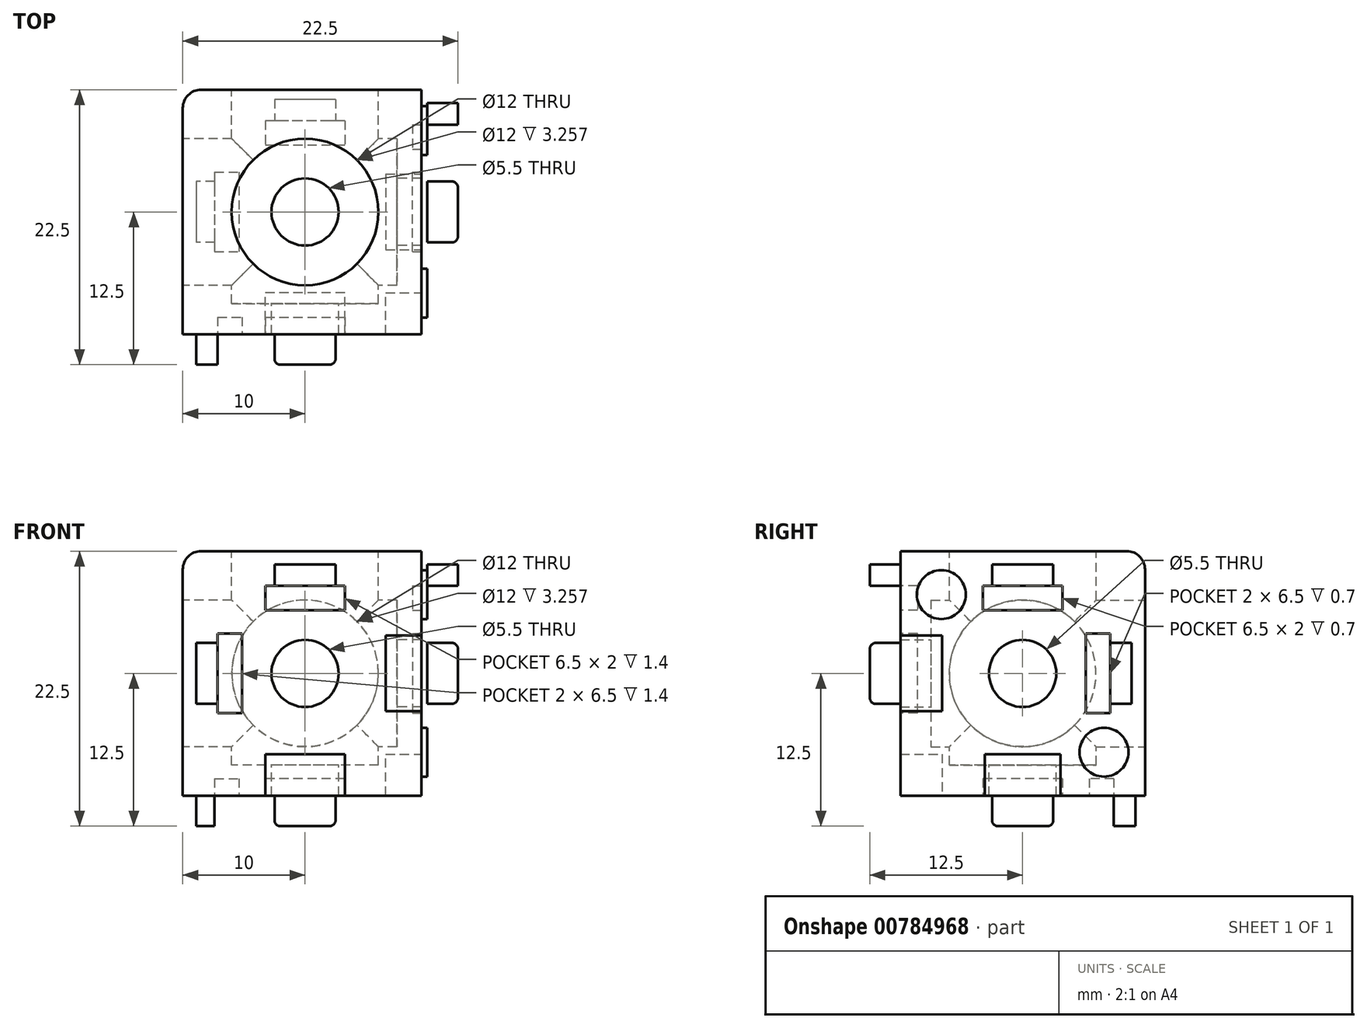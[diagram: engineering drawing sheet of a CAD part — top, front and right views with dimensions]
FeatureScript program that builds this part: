
annotation { "Feature Type Name" : "Feature", "Feature Type Description" : "" }
export const myFeature = defineFeature(function(context is Context, id is Id, definition is map)
    precondition{}
    {
        {
            var Q0;
            Q0=qCreatedBy(makeId("Top.planeOp"),FACE);
            var sketch = newSketch(context, id + "F0", { "sketchPlane" : qUnion([Q0])});
            skLineSegment(sketch, "E0.bottom", {"start": v(10, -10) * mm, "end": v(-10, -10) * mm});
            skLineSegment(sketch, "E0.top", {"start": v(10, 10) * mm, "end": v(-10, 10) * mm});
            skLineSegment(sketch, "E0.left", {"start": v(10, -10) * mm, "end": v(10, 10) * mm});
            skLineSegment(sketch, "E0.right", {"start": v(-10, -10) * mm, "end": v(-10, 10) * mm});
            skPoint(sketch, "E0.middle", {"position": v(0, 0) * mm});
            skLineSegment(sketch, "E1", {"start": v(-10, 10) * mm, "end": v(10, -10) * mm, "construction": true});
            skLineSegment(sketch, "E2", {"start": v(10, 10) * mm, "end": v(-10, -10) * mm, "construction": true});
            skSolve(sketch);
        }
        {
            var Q0;
            Q0=makeQuery(id+"F0.imprint","IMPRINT",FACE,{"disambiguationData":[TD([[makeQuery(id+"F0.imprint","IMPRINT",EDGE,{"derivedFrom":sQuery(id+"F0.wireOp",EDGE,"E0.bottom")}),-1.0]])]});
            extrude(context, id + "F1", {"entities" : qUnion([Q0]), "endBound" : BoundingType.SYMMETRIC, "depth" : 20 * mm, "offsetDistance" : 25 * mm});
        }
        {
            var Q0;
            Q0=makeQuery(id+"F1.opExtrude","CAP_FACE",FACE,{"disambiguationData":[OSD([sQuery(id+"F0.wireOp",EDGE,"E0.bottom"),sQuery(id+"F0.wireOp",EDGE,"E0.top"),sQuery(id+"F0.wireOp",EDGE,"E0.left"),sQuery(id+"F0.wireOp",EDGE,"E0.right")])],"isStart":false});
            var sketch = newSketch(context, id + "F2", { "sketchPlane" : qUnion([Q0])});
            skCircle(sketch, "E3", {"center": v(0, 0) * mm, "radius": 6 * mm});
            skLineSegment(sketch, "E4", {"start": v(-10, 10) * mm, "end": v(10, -10) * mm, "construction": true});
            skLineSegment(sketch, "E5", {"start": v(10, 10) * mm, "end": v(-10, -10) * mm, "construction": true});
            skSolve(sketch);
        }
        {
            var Q0;
            Q0=makeQuery(id+"F2.imprint","IMPRINT",FACE,{"disambiguationData":[TD([[makeQuery(id+"F2.imprint","IMPRINT",EDGE,{"derivedFrom":sQuery(id+"F2.wireOp",EDGE,"E3")}),1.0]])]});
            extrude(context, id + "F3", {"entities" : qUnion([Q0]), "operationType" : NewBodyOperationType.REMOVE, "oppositeDirection" : true, "depth" : 17.5 * mm, "offsetDistance" : 25 * mm});
        }
        {
            var Q0;
            Q0=makeQuery(id+"F1.opExtrude","SWEPT_FACE",FACE,{"disambiguationData":[OSD([sQuery(id+"F0.wireOp",EDGE,"E0.top")])]});
            var sketch = newSketch(context, id + "F4", { "sketchPlane" : qUnion([Q0])});
            skCircle(sketch, "E6", {"center": v(0, 0) * mm, "radius": 6 * mm});
            skLineSegment(sketch, "E7", {"start": v(-10, 10) * mm, "end": v(10, -10) * mm, "construction": true});
            skLineSegment(sketch, "E8", {"start": v(-10, -10) * mm, "end": v(10, 10) * mm, "construction": true});
            skSolve(sketch);
        }
        {
            var Q0;
            Q0=makeQuery(id+"F4.imprint","IMPRINT",FACE,{"disambiguationData":[TD([[makeQuery(id+"F4.imprint","IMPRINT",EDGE,{"derivedFrom":sQuery(id+"F4.wireOp",EDGE,"E6")}),1.0]])]});
            extrude(context, id + "F5", {"entities" : qUnion([Q0]), "operationType" : NewBodyOperationType.REMOVE, "oppositeDirection" : true, "depth" : 17.5 * mm, "offsetDistance" : 25 * mm});
        }
        {
            var Q0;
            Q0=makeQuery(id+"F1.opExtrude","SWEPT_FACE",FACE,{"disambiguationData":[OSD([sQuery(id+"F0.wireOp",EDGE,"E0.right")])]});
            var sketch = newSketch(context, id + "F6", { "sketchPlane" : qUnion([Q0])});
            skCircle(sketch, "E9", {"center": v(0, 0) * mm, "radius": 6 * mm});
            skLineSegment(sketch, "E10", {"start": v(-10, 10) * mm, "end": v(10, -10) * mm, "construction": true});
            skLineSegment(sketch, "E11", {"start": v(10, 10) * mm, "end": v(-10, -10) * mm});
            skSolve(sketch);
        }
        {
            var Q0;
            Q0=makeQuery(id+"F6.imprint","IMPRINT",FACE,{"disambiguationData":[TD([[makeQuery(id+"F6.imprint","IMPRINT",EDGE,{"derivedFrom":sQuery(id+"F6.wireOp",EDGE,"E9")}),1.0]])]});
            extrude(context, id + "F7", {"entities" : qUnion([Q0]), "operationType" : NewBodyOperationType.REMOVE, "oppositeDirection" : true, "depth" : 17.5 * mm, "offsetDistance" : 25 * mm});
        }
        {
            var Q0;
            Q0=makeQuery(id+"F3.boolean.opBoolean","COPY",FACE,{"derivedFrom":makeQuery(id+"F3.opExtrude","CAP_FACE",FACE,{"disambiguationData":[OSD([sQuery(id+"F2.wireOp",EDGE,"E3")])],"isStart":false})});
            var sketch = newSketch(context, id + "F8", { "sketchPlane" : qUnion([Q0])});
            skPoint(sketch, "E12", {"position": v(0, 0) * mm});
            skSolve(sketch);
        }
        {
            var Q0;
            Q0=sQuery(id+"F8.wireOp",VERTEX,"E12");
            var Q1;
            Q1=makeQuery(id+"F1.opExtrude","SWEPT_BODY",BODY,{"disambiguationData":[OSD([sQuery(id+"F0.wireOp",EDGE,"E0.bottom"),sQuery(id+"F0.wireOp",EDGE,"E0.top"),sQuery(id+"F0.wireOp",EDGE,"E0.left"),sQuery(id+"F0.wireOp",EDGE,"E0.right")])]});
            hole(context, id + "F9", {"style" : HoleStyle.SIMPLE, "endStyle" : HoleEndStyle.THROUGH, "holeDiameter" : 5.5 * mm, "majorDiameter" : 5 * mm, "isTappedThrough" : true, "tappedDepth" : 12 * mm, "tapClearance" : 3, "locations" : qUnion([Q0]), "scope" : qUnion([Q1])});
        }
        {
            var Q0;
            Q0=makeQuery(id+"F5.boolean.opBoolean","COPY",FACE,{"derivedFrom":makeQuery(id+"F5.opExtrude","CAP_FACE",FACE,{"disambiguationData":[OSD([sQuery(id+"F4.wireOp",EDGE,"E6")])],"isStart":false})});
            var sketch = newSketch(context, id + "F10", { "sketchPlane" : qUnion([Q0])});
            skPoint(sketch, "E13", {"position": v(0, 0) * mm});
            skSolve(sketch);
        }
        {
            var Q0;
            Q0=sQuery(id+"F10.wireOp",VERTEX,"E13");
            var Q1;
            Q1=makeQuery(id+"F1.opExtrude","SWEPT_BODY",BODY,{"disambiguationData":[OSD([sQuery(id+"F0.wireOp",EDGE,"E0.bottom"),sQuery(id+"F0.wireOp",EDGE,"E0.top"),sQuery(id+"F0.wireOp",EDGE,"E0.left"),sQuery(id+"F0.wireOp",EDGE,"E0.right")])]});
            hole(context, id + "F11", {"style" : HoleStyle.SIMPLE, "endStyle" : HoleEndStyle.THROUGH, "holeDiameter" : 5.5 * mm, "majorDiameter" : 5 * mm, "isTappedThrough" : true, "tappedDepth" : 12 * mm, "tapClearance" : 3, "locations" : qUnion([Q0]), "scope" : qUnion([Q1])});
        }
        {
            var Q0;
            Q0=makeQuery(id+"F7.boolean.opBoolean","COPY",FACE,{"derivedFrom":makeQuery(id+"F7.opExtrude","CAP_FACE",FACE,{"disambiguationData":[OSD([sQuery(id+"F6.wireOp",EDGE,"E9")])],"isStart":false})});
            var sketch = newSketch(context, id + "F12", { "sketchPlane" : qUnion([Q0])});
            skPoint(sketch, "E14", {"position": v(0, 0) * mm});
            skSolve(sketch);
        }
        {
            var Q0;
            Q0=sQuery(id+"F12.wireOp",VERTEX,"E14");
            var Q1;
            Q1=makeQuery(id+"F1.opExtrude","SWEPT_BODY",BODY,{"disambiguationData":[OSD([sQuery(id+"F0.wireOp",EDGE,"E0.bottom"),sQuery(id+"F0.wireOp",EDGE,"E0.top"),sQuery(id+"F0.wireOp",EDGE,"E0.left"),sQuery(id+"F0.wireOp",EDGE,"E0.right")])]});
            hole(context, id + "F13", {"style" : HoleStyle.SIMPLE, "endStyle" : HoleEndStyle.THROUGH, "holeDiameter" : 5.5 * mm, "majorDiameter" : 5 * mm, "isTappedThrough" : true, "tappedDepth" : 12 * mm, "tapClearance" : 3, "locations" : qUnion([Q0]), "scope" : qUnion([Q1])});
        }
        {
            var Q0;
            Q0=makeQuery(id+"F1.opExtrude","SWEPT_FACE",FACE,{"disambiguationData":[OSD([sQuery(id+"F0.wireOp",EDGE,"E0.left")])]});
            var sketch = newSketch(context, id + "F14", { "sketchPlane" : qUnion([Q0])});
            skLineSegment(sketch, "E15", {"start": v(10, 0) * mm, "end": v(-10, 0) * mm, "construction": true});
            skLineSegment(sketch, "E16", {"start": v(0, 10) * mm, "end": v(0, -10) * mm, "construction": true});
            skCircle(sketch, "E17", {"center": v(6.65, 6.45) * mm, "radius": 2 * mm});
            skCircle(sketch, "E18.MirrorC", {"center": v(6.65, -6.45) * mm, "radius": 2 * mm});
            skCircle(sketch, "E19.MirrorC", {"center": v(-6.65, -6.45) * mm, "radius": 2 * mm});
            skCircle(sketch, "E20.MirrorC", {"center": v(-6.65, 6.45) * mm, "radius": 2 * mm});
            skSolve(sketch);
        }
        {
            var Q0;
            Q0=makeQuery(id+"F14.imprint","IMPRINT",FACE,{"disambiguationData":[TD([[makeQuery(id+"F14.imprint","IMPRINT",EDGE,{"derivedFrom":sQuery(id+"F14.wireOp",EDGE,"E17")}),1.0]])]});
            var Q1;
            Q1=makeQuery(id+"F14.imprint","IMPRINT",FACE,{"disambiguationData":[TD([[makeQuery(id+"F14.imprint","IMPRINT",EDGE,{"derivedFrom":sQuery(id+"F14.wireOp",EDGE,"E18.MirrorC")}),-1.0]])]});
            var Q2;
            Q2=makeQuery(id+"F14.imprint","IMPRINT",FACE,{"disambiguationData":[TD([[makeQuery(id+"F14.imprint","IMPRINT",EDGE,{"derivedFrom":sQuery(id+"F14.wireOp",EDGE,"E19.MirrorC")}),1.0]])]});
            var Q3;
            Q3=makeQuery(id+"F14.imprint","IMPRINT",FACE,{"disambiguationData":[TD([[makeQuery(id+"F14.imprint","IMPRINT",EDGE,{"derivedFrom":sQuery(id+"F14.wireOp",EDGE,"E20.MirrorC")}),-1.0]])]});
            extrude(context, id + "F15", {"entities" : qUnion([Q0, Q1, Q2, Q3]), "operationType" : NewBodyOperationType.REMOVE, "oppositeDirection" : true, "depth" : 0.5 * mm, "offsetDistance" : 25 * mm});
        }
        {
            var Q0;
            Q0=makeQuery(id+"F1.opExtrude","SWEPT_FACE",FACE,{"disambiguationData":[OSD([sQuery(id+"F0.wireOp",EDGE,"E0.left")])]});
            var sketch = newSketch(context, id + "F16", { "sketchPlane" : qUnion([Q0])});
            skLineSegment(sketch, "E21.bottom", {"start": v(7.15, -2.5) * mm, "end": v(8.9, -2.5) * mm});
            skLineSegment(sketch, "E21.top", {"start": v(7.15, 2.5) * mm, "end": v(8.9, 2.5) * mm});
            skLineSegment(sketch, "E21.left", {"start": v(7.15, -2.5) * mm, "end": v(7.15, 2.5) * mm});
            skLineSegment(sketch, "E21.right", {"start": v(8.9, -2.5) * mm, "end": v(8.9, 2.5) * mm});
            skPoint(sketch, "E21.middle", {"position": v(8.03, 0) * mm});
            skPoint(sketch, "E21.middle.positionSnap0", {"position": v(10, 0) * mm});
            skPoint(sketch, "E21.centerSnap0", {"position": v(10, 0) * mm});
            skLineSegment(sketch, "E22.bottom", {"start": v(-2.5, 7.15) * mm, "end": v(2.5, 7.15) * mm});
            skLineSegment(sketch, "E22.top", {"start": v(-2.5, 8.9) * mm, "end": v(2.5, 8.9) * mm});
            skLineSegment(sketch, "E22.left", {"start": v(-2.5, 7.15) * mm, "end": v(-2.5, 8.9) * mm});
            skLineSegment(sketch, "E22.right", {"start": v(2.5, 7.15) * mm, "end": v(2.5, 8.9) * mm});
            skPoint(sketch, "E22.middle", {"position": v(0, 8.02) * mm});
            skPoint(sketch, "E22.middle.positionSnap0", {"position": v(0, 10) * mm});
            skPoint(sketch, "E22.centerSnap0", {"position": v(0, 10) * mm});
            skSolve(sketch);
        }
        {
            var Q0;
            Q0 = qSketchRegion(id + "F16", true);
            extrude(context, id + "F17", {"entities" : qUnion([Q0]), "operationType" : NewBodyOperationType.ADD, "depth" : 2.5 * mm, "offsetDistance" : 25 * mm});
        }
        {
            var Q0;
            Q0=makeQuery(id+"F1.opExtrude","SWEPT_FACE",FACE,{"disambiguationData":[OSD([sQuery(id+"F0.wireOp",EDGE,"E0.left")])]});
            var sketch = newSketch(context, id + "F18", { "sketchPlane" : qUnion([Q0])});
            skLineSegment(sketch, "E23.bottom", {"start": v(7.15, 3.25) * mm, "end": v(5.15, 3.25) * mm});
            skLineSegment(sketch, "E23.top", {"start": v(7.15, -3.25) * mm, "end": v(5.15, -3.25) * mm});
            skLineSegment(sketch, "E23.left", {"start": v(7.15, 3.25) * mm, "end": v(7.15, -3.25) * mm});
            skLineSegment(sketch, "E23.right", {"start": v(5.15, 3.25) * mm, "end": v(5.15, -3.25) * mm});
            skLineSegment(sketch, "E24.bottom", {"start": v(-3.25, 7.15) * mm, "end": v(3.25, 7.15) * mm});
            skLineSegment(sketch, "E24.top", {"start": v(-3.25, 5.15) * mm, "end": v(3.25, 5.15) * mm});
            skLineSegment(sketch, "E24.left", {"start": v(-3.25, 7.15) * mm, "end": v(-3.25, 5.15) * mm});
            skLineSegment(sketch, "E24.right", {"start": v(3.25, 7.15) * mm, "end": v(3.25, 5.15) * mm});
            skSolve(sketch);
        }
        {
            var Q0;
            Q0=makeQuery(id+"F18.imprint","IMPRINT",FACE,{"disambiguationData":[TD([[makeQuery(id+"F18.imprint","IMPRINT",EDGE,{"derivedFrom":sQuery(id+"F18.wireOp",EDGE,"E24.top")}),1.0]])]});
            var Q1;
            {var subQ3=sQuery(id+"F18.wireOp",EDGE,"E23.bottom");Q1=makeQuery(id+"F18.imprint","IMPRINT",FACE,{"disambiguationData":[TD([[makeQuery(id+"F18.imprint","IMPRINT",EDGE,{"derivedFrom":subQ3}),1.0]])]});}
            extrude(context, id + "F19", {"entities" : qUnion([Q0, Q1]), "operationType" : NewBodyOperationType.REMOVE, "oppositeDirection" : true, "depth" : 1.2 * mm, "offsetDistance" : 25 * mm});
        }
        {
            var Q0;
            Q0=makeQuery(id+"F1.opExtrude","SWEPT_FACE",FACE,{"disambiguationData":[OSD([sQuery(id+"F0.wireOp",EDGE,"E0.left")])]});
            var sketch = newSketch(context, id + "F20", { "sketchPlane" : qUnion([Q0])});
            skLineSegment(sketch, "E25.bottom", {"start": v(3.1, -10) * mm, "end": v(-3.1, -10) * mm});
            skLineSegment(sketch, "E25.top", {"start": v(3.1, -6.6) * mm, "end": v(-3.1, -6.6) * mm});
            skLineSegment(sketch, "E25.left", {"start": v(3.1, -10) * mm, "end": v(3.1, -6.6) * mm});
            skLineSegment(sketch, "E25.right", {"start": v(-3.1, -10) * mm, "end": v(-3.1, -6.6) * mm});
            skLineSegment(sketch, "E26.bottom", {"start": v(-10, -3.1) * mm, "end": v(-6.6, -3.1) * mm});
            skLineSegment(sketch, "E26.top", {"start": v(-10, 3.1) * mm, "end": v(-6.6, 3.1) * mm});
            skLineSegment(sketch, "E26.left", {"start": v(-10, -3.1) * mm, "end": v(-10, 3.1) * mm});
            skLineSegment(sketch, "E26.right", {"start": v(-6.6, -3.1) * mm, "end": v(-6.6, 3.1) * mm});
            skSolve(sketch);
        }
        {
            var Q0;
            Q0 = qSketchRegion(id + "F20", true);
            extrude(context, id + "F21", {"entities" : qUnion([Q0]), "operationType" : NewBodyOperationType.REMOVE, "oppositeDirection" : true, "depth" : 3.4 * mm, "offsetDistance" : 25 * mm});
        }
        {
            var Q0;
            Q0=makeQuery(id+"F17.opExtrude","CAP_EDGE",EDGE,{"disambiguationData":[OSD([sQuery(id+"F16.wireOp",EDGE,"E22.left")])],"isStart":false});
            var Q1;
            Q1=makeQuery(id+"F17.opExtrude","CAP_EDGE",EDGE,{"disambiguationData":[OSD([sQuery(id+"F16.wireOp",EDGE,"E22.right")])],"isStart":false});
            var Q2;
            Q2=makeQuery(id+"F17.opExtrude","CAP_EDGE",EDGE,{"disambiguationData":[OSD([sQuery(id+"F16.wireOp",EDGE,"E21.top")])],"isStart":false});
            var Q3;
            Q3=makeQuery(id+"F17.opExtrude","CAP_EDGE",EDGE,{"disambiguationData":[OSD([sQuery(id+"F16.wireOp",EDGE,"E21.bottom")])],"isStart":false});
            fillet(context, id + "F22", {"entities" : qUnion([Q0, Q1, Q2, Q3]), "radius" : 0.5 * mm, "tangentPropagation" : true, "allowEdgeOverflow" : false});
        }
        {
            var Q0;
            Q0=makeQuery(id+"F1.opExtrude","CAP_FACE",FACE,{"disambiguationData":[OSD([sQuery(id+"F0.wireOp",EDGE,"E0.bottom"),sQuery(id+"F0.wireOp",EDGE,"E0.top"),sQuery(id+"F0.wireOp",EDGE,"E0.left"),sQuery(id+"F0.wireOp",EDGE,"E0.right")])],"isStart":true});
            var sketch = newSketch(context, id + "F23", { "sketchPlane" : qUnion([Q0])});
            skLineSegment(sketch, "E27", {"start": v(0, -10) * mm, "end": v(0, 10) * mm, "construction": true});
            skLineSegment(sketch, "E28", {"start": v(-10, 0) * mm, "end": v(6.6, 0) * mm, "construction": true});
            skLineSegment(sketch, "E29.bottom", {"start": v(2.5, -9.2) * mm, "end": v(-2.5, -9.2) * mm});
            skLineSegment(sketch, "E29.top", {"start": v(2.5, -7.46) * mm, "end": v(-2.5, -7.46) * mm});
            skLineSegment(sketch, "E29.left", {"start": v(2.5, -9.2) * mm, "end": v(2.5, -7.46) * mm});
            skLineSegment(sketch, "E29.right", {"start": v(-2.5, -9.2) * mm, "end": v(-2.5, -7.46) * mm});
            skLineSegment(sketch, "E30.bottom", {"start": v(-3.25, -7.46) * mm, "end": v(3.25, -7.46) * mm});
            skLineSegment(sketch, "E30.top", {"start": v(-3.25, -5.46) * mm, "end": v(3.25, -5.46) * mm});
            skLineSegment(sketch, "E30.left", {"start": v(-3.25, -7.46) * mm, "end": v(-3.25, -5.46) * mm});
            skLineSegment(sketch, "E30.right", {"start": v(3.25, -7.46) * mm, "end": v(3.25, -5.46) * mm});
            skSolve(sketch);
        }
        {
            var Q0;
            Q0=makeQuery(id+"F23.imprint","IMPRINT",FACE,{"disambiguationData":[TD([[makeQuery(id+"F23.imprint","IMPRINT",EDGE,{"derivedFrom":sQuery(id+"F23.wireOp",EDGE,"E29.bottom")}),-1.0]])]});
            extrude(context, id + "F24", {"entities" : qUnion([Q0]), "operationType" : NewBodyOperationType.ADD, "depth" : 2.5 * mm, "offsetDistance" : 25 * mm});
        }
        {
            var Q0;
            Q0=makeQuery(id+"F1.opExtrude","CAP_FACE",FACE,{"disambiguationData":[OSD([sQuery(id+"F0.wireOp",EDGE,"E0.bottom"),sQuery(id+"F0.wireOp",EDGE,"E0.top"),sQuery(id+"F0.wireOp",EDGE,"E0.left"),sQuery(id+"F0.wireOp",EDGE,"E0.right")])],"isStart":true});
            var sketch = newSketch(context, id + "F25", { "sketchPlane" : qUnion([Q0])});
            skLineSegment(sketch, "E31.bottom", {"start": v(3.25, -7.46) * mm, "end": v(-3.25, -7.46) * mm});
            skLineSegment(sketch, "E31.top", {"start": v(3.25, -5.46) * mm, "end": v(-3.25, -5.46) * mm});
            skLineSegment(sketch, "E31.left", {"start": v(3.25, -7.46) * mm, "end": v(3.25, -5.46) * mm});
            skLineSegment(sketch, "E31.right", {"start": v(-3.25, -7.46) * mm, "end": v(-3.25, -5.46) * mm});
            skSolve(sketch);
        }
        {
            var Q0;
            Q0=makeQuery(id+"F25.imprint","IMPRINT",FACE,{"disambiguationData":[TD([[makeQuery(id+"F25.imprint","IMPRINT",EDGE,{"derivedFrom":sQuery(id+"F25.wireOp",EDGE,"E31.top")}),1.0]])]});
            extrude(context, id + "F26", {"entities" : qUnion([Q0]), "operationType" : NewBodyOperationType.REMOVE, "oppositeDirection" : true, "depth" : 1.4 * mm, "offsetDistance" : 25 * mm});
        }
        {
            var Q0;
            Q0=makeQuery(id+"F1.opExtrude","CAP_FACE",FACE,{"disambiguationData":[OSD([sQuery(id+"F0.wireOp",EDGE,"E0.bottom"),sQuery(id+"F0.wireOp",EDGE,"E0.top"),sQuery(id+"F0.wireOp",EDGE,"E0.left"),sQuery(id+"F0.wireOp",EDGE,"E0.right")])],"isStart":true});
            var sketch = newSketch(context, id + "F27", { "sketchPlane" : qUnion([Q0])});
            skLineSegment(sketch, "E32.bottom", {"start": v(-7.4, -2.5) * mm, "end": v(-8.9, -2.5) * mm});
            skLineSegment(sketch, "E32.top", {"start": v(-7.4, 2.5) * mm, "end": v(-8.9, 2.5) * mm});
            skLineSegment(sketch, "E32.left", {"start": v(-7.4, -2.5) * mm, "end": v(-7.4, 2.5) * mm});
            skLineSegment(sketch, "E32.right", {"start": v(-8.9, -2.5) * mm, "end": v(-8.9, 2.5) * mm});
            skSolve(sketch);
        }
        {
            var Q0;
            Q0=makeQuery(id+"F27.imprint","IMPRINT",FACE,{"disambiguationData":[TD([[makeQuery(id+"F27.imprint","IMPRINT",EDGE,{"derivedFrom":sQuery(id+"F27.wireOp",EDGE,"E32.bottom")}),-1.0]])]});
            extrude(context, id + "F28", {"entities" : qUnion([Q0]), "operationType" : NewBodyOperationType.ADD, "depth" : 2.5 * mm, "offsetDistance" : 25 * mm});
        }
        {
            var Q0;
            Q0=makeQuery(id+"F1.opExtrude","CAP_FACE",FACE,{"disambiguationData":[OSD([sQuery(id+"F0.wireOp",EDGE,"E0.bottom"),sQuery(id+"F0.wireOp",EDGE,"E0.top"),sQuery(id+"F0.wireOp",EDGE,"E0.left"),sQuery(id+"F0.wireOp",EDGE,"E0.right")])],"isStart":true});
            var sketch = newSketch(context, id + "F29", { "sketchPlane" : qUnion([Q0])});
            skLineSegment(sketch, "E33.bottom", {"start": v(-7.4, -3.25) * mm, "end": v(-5.4, -3.25) * mm});
            skLineSegment(sketch, "E33.top", {"start": v(-7.4, 3.25) * mm, "end": v(-5.4, 3.25) * mm});
            skLineSegment(sketch, "E33.left", {"start": v(-7.4, -3.25) * mm, "end": v(-7.4, 3.25) * mm});
            skLineSegment(sketch, "E33.right", {"start": v(-5.4, -3.25) * mm, "end": v(-5.4, 3.25) * mm});
            skSolve(sketch);
        }
        {
            var Q0;
            {var subQ3=sQuery(id+"F29.wireOp",EDGE,"E33.bottom");Q0=makeQuery(id+"F29.imprint","IMPRINT",FACE,{"disambiguationData":[TD([[makeQuery(id+"F29.imprint","IMPRINT",EDGE,{"derivedFrom":subQ3}),1.0]])]});}
            extrude(context, id + "F30", {"entities" : qUnion([Q0]), "operationType" : NewBodyOperationType.REMOVE, "oppositeDirection" : true, "depth" : 1.4 * mm, "offsetDistance" : 25 * mm});
        }
        {
            var Q0;
            Q0=makeQuery(id+"F1.opExtrude","CAP_FACE",FACE,{"disambiguationData":[OSD([sQuery(id+"F0.wireOp",EDGE,"E0.bottom"),sQuery(id+"F0.wireOp",EDGE,"E0.top"),sQuery(id+"F0.wireOp",EDGE,"E0.left"),sQuery(id+"F0.wireOp",EDGE,"E0.right")])],"isStart":true});
            var sketch = newSketch(context, id + "F31", { "sketchPlane" : qUnion([Q0])});
            skLineSegment(sketch, "E34.bottom", {"start": v(3.25, 10) * mm, "end": v(-3.25, 10) * mm});
            skLineSegment(sketch, "E34.top", {"start": v(3.25, 6.6) * mm, "end": v(-3.25, 6.6) * mm});
            skLineSegment(sketch, "E34.left", {"start": v(3.25, 10) * mm, "end": v(3.25, 6.6) * mm});
            skLineSegment(sketch, "E34.right", {"start": v(-3.25, 10) * mm, "end": v(-3.25, 6.6) * mm});
            skSolve(sketch);
        }
        {
            var Q0;
            Q0=makeQuery(id+"F31.imprint","IMPRINT",FACE,{"disambiguationData":[TD([[makeQuery(id+"F31.imprint","IMPRINT",EDGE,{"derivedFrom":sQuery(id+"F31.wireOp",EDGE,"E34.bottom")}),1.0]])]});
            extrude(context, id + "F32", {"entities" : qUnion([Q0]), "operationType" : NewBodyOperationType.REMOVE, "oppositeDirection" : true, "depth" : 3.4 * mm, "offsetDistance" : 25 * mm});
        }
        {
            var Q0;
            Q0=makeQuery(id+"F1.opExtrude","SWEPT_FACE",FACE,{"disambiguationData":[OSD([sQuery(id+"F0.wireOp",EDGE,"E0.bottom")])]});
            var sketch = newSketch(context, id + "F33", { "sketchPlane" : qUnion([Q0])});
            skLineSegment(sketch, "E35.bottom", {"start": v(-7.15, -2.5) * mm, "end": v(-8.9, -2.5) * mm});
            skLineSegment(sketch, "E35.top", {"start": v(-7.15, 2.5) * mm, "end": v(-8.9, 2.5) * mm});
            skLineSegment(sketch, "E35.left", {"start": v(-7.15, -2.5) * mm, "end": v(-7.15, 2.5) * mm});
            skLineSegment(sketch, "E35.right", {"start": v(-8.9, -2.5) * mm, "end": v(-8.9, 2.5) * mm});
            skLineSegment(sketch, "E36.bottom", {"start": v(2.5, 7.15) * mm, "end": v(-2.5, 7.15) * mm});
            skLineSegment(sketch, "E36.top", {"start": v(2.5, 8.9) * mm, "end": v(-2.5, 8.9) * mm});
            skLineSegment(sketch, "E36.left", {"start": v(2.5, 7.15) * mm, "end": v(2.5, 8.9) * mm});
            skLineSegment(sketch, "E36.right", {"start": v(-2.5, 7.15) * mm, "end": v(-2.5, 8.9) * mm});
            skSolve(sketch);
        }
        {
            var Q0;
            Q0=makeQuery(id+"F33.imprint","IMPRINT",FACE,{"disambiguationData":[TD([[makeQuery(id+"F33.imprint","IMPRINT",EDGE,{"derivedFrom":sQuery(id+"F33.wireOp",EDGE,"E35.bottom")}),1.0]])]});
            var sketch = newSketch(context, id + "F34", { "sketchPlane" : qUnion([Q0])});
            skSolve(sketch);
        }
        {
            var Q0;
            Q0=makeQuery(id+"F33.imprint","IMPRINT",FACE,{"disambiguationData":[TD([[makeQuery(id+"F33.imprint","IMPRINT",EDGE,{"derivedFrom":sQuery(id+"F33.wireOp",EDGE,"E36.bottom")}),-1.0]])]});
            var Q1;
            Q1=makeQuery(id+"F34.imprint","IMPRINT",FACE,{"disambiguationData":[TD([[makeQuery(id+"F34.imprint","IMPRINT",EDGE,{"derivedFrom":makeQuery(id+"F33.imprint","IMPRINT",EDGE,{"derivedFrom":sQuery(id+"F33.wireOp",EDGE,"E36.bottom")})}),-1.0]])]});
            var Q2;
            Q2=makeQuery(id+"F33.imprint","IMPRINT",FACE,{"disambiguationData":[TD([[makeQuery(id+"F33.imprint","IMPRINT",EDGE,{"derivedFrom":sQuery(id+"F33.wireOp",EDGE,"E35.bottom")}),-1.0]])]});
            extrude(context, id + "F35", {"entities" : qUnion([Q0, Q1, Q2]), "operationType" : NewBodyOperationType.ADD, "depth" : 2.5 * mm, "offsetDistance" : 25 * mm});
        }
        {
            var Q0;
            Q0=makeQuery(id+"F1.opExtrude","SWEPT_FACE",FACE,{"disambiguationData":[OSD([sQuery(id+"F0.wireOp",EDGE,"E0.bottom")])]});
            var sketch = newSketch(context, id + "F36", { "sketchPlane" : qUnion([Q0])});
            skLineSegment(sketch, "E37.bottom", {"start": v(-7.15, 3.25) * mm, "end": v(-5.15, 3.25) * mm});
            skLineSegment(sketch, "E37.top", {"start": v(-7.15, -3.25) * mm, "end": v(-5.15, -3.25) * mm});
            skLineSegment(sketch, "E37.left", {"start": v(-7.15, 3.25) * mm, "end": v(-7.15, -3.25) * mm});
            skLineSegment(sketch, "E37.right", {"start": v(-5.15, 3.25) * mm, "end": v(-5.15, -3.25) * mm});
            skLineSegment(sketch, "E38.bottom", {"start": v(-3.25, 7.15) * mm, "end": v(3.25, 7.15) * mm});
            skLineSegment(sketch, "E38.top", {"start": v(-3.25, 5.15) * mm, "end": v(3.25, 5.15) * mm});
            skLineSegment(sketch, "E38.left", {"start": v(-3.25, 7.15) * mm, "end": v(-3.25, 5.15) * mm});
            skLineSegment(sketch, "E38.right", {"start": v(3.25, 7.15) * mm, "end": v(3.25, 5.15) * mm});
            skSolve(sketch);
        }
        {
            var Q0;
            {var subQ3=sQuery(id+"F36.wireOp",EDGE,"E37.bottom");Q0=makeQuery(id+"F36.imprint","IMPRINT",FACE,{"disambiguationData":[TD([[makeQuery(id+"F36.imprint","IMPRINT",EDGE,{"derivedFrom":subQ3}),-1.0]])]});}
            var Q1;
            Q1=makeQuery(id+"F36.imprint","IMPRINT",FACE,{"disambiguationData":[TD([[makeQuery(id+"F36.imprint","IMPRINT",EDGE,{"derivedFrom":sQuery(id+"F36.wireOp",EDGE,"E38.top")}),1.0]])]});
            extrude(context, id + "F37", {"entities" : qUnion([Q0, Q1]), "operationType" : NewBodyOperationType.REMOVE, "oppositeDirection" : true, "depth" : 1.4 * mm, "offsetDistance" : 25 * mm});
        }
        {
            var Q0;
            {var subQ0=sQuery(id+"F33.wireOp",EDGE,"E36.left");Q0=makeQuery(id+"F35.opExtrude","CAP_EDGE",EDGE,{"disambiguationData":[OSD([subQ0]),TDD([makeQuery(id+"F33.imprint","IMPRINT",EDGE,{"derivedFrom":subQ0})])],"isStart":false});}
            var Q1;
            {var subQ0=sQuery(id+"F33.wireOp",EDGE,"E36.right");Q1=makeQuery(id+"F35.opExtrude","CAP_EDGE",EDGE,{"disambiguationData":[OSD([subQ0]),TDD([makeQuery(id+"F33.imprint","IMPRINT",EDGE,{"derivedFrom":subQ0})])],"isStart":false});}
            var Q2;
            Q2=makeQuery(id+"F35.opExtrude","CAP_EDGE",EDGE,{"disambiguationData":[OSD([sQuery(id+"F33.wireOp",EDGE,"E35.top")])],"isStart":false});
            var Q3;
            Q3=makeQuery(id+"F35.opExtrude","CAP_EDGE",EDGE,{"disambiguationData":[OSD([sQuery(id+"F33.wireOp",EDGE,"E35.bottom")])],"isStart":false});
            var Q4;
            Q4=makeQuery(id+"F24.opExtrude","CAP_EDGE",EDGE,{"disambiguationData":[OSD([sQuery(id+"F23.wireOp",EDGE,"E29.left")])],"isStart":false});
            var Q5;
            Q5=makeQuery(id+"F24.opExtrude","CAP_EDGE",EDGE,{"disambiguationData":[OSD([sQuery(id+"F23.wireOp",EDGE,"E29.right")])],"isStart":false});
            var Q6;
            Q6=makeQuery(id+"F28.opExtrude","CAP_EDGE",EDGE,{"disambiguationData":[OSD([sQuery(id+"F27.wireOp",EDGE,"E32.bottom")])],"isStart":false});
            var Q7;
            Q7=makeQuery(id+"F28.opExtrude","CAP_EDGE",EDGE,{"disambiguationData":[OSD([sQuery(id+"F27.wireOp",EDGE,"E32.top")])],"isStart":false});
            fillet(context, id + "F38", {"entities" : qUnion([Q0, Q1, Q2, Q3, Q4, Q5, Q6, Q7]), "radius" : 0.5 * mm, "tangentPropagation" : true, "allowEdgeOverflow" : false});
        }
        {
            var Q0;
            Q0=makeQuery(id+"F1.opExtrude","SWEPT_EDGE",EDGE,{"disambiguationData":[OSD([sQuery(id+"F0.wireOp",EDGE,"E0.top"),sQuery(id+"F0.wireOp",EDGE,"E0.right")])]});
            var Q1;
            Q1=makeQuery(id+"F1.opExtrude","CAP_EDGE",EDGE,{"disambiguationData":[OSD([sQuery(id+"F0.wireOp",EDGE,"E0.top")])],"isStart":false});
            var Q2;
            Q2=makeQuery(id+"F1.opExtrude","CAP_EDGE",EDGE,{"disambiguationData":[OSD([sQuery(id+"F0.wireOp",EDGE,"E0.right")])],"isStart":false});
            fillet(context, id + "F39", {"entities" : qUnion([Q0, Q1, Q2]), "radius" : 1.5 * mm, "tangentPropagation" : true, "allowEdgeOverflow" : false});
        }
    });
